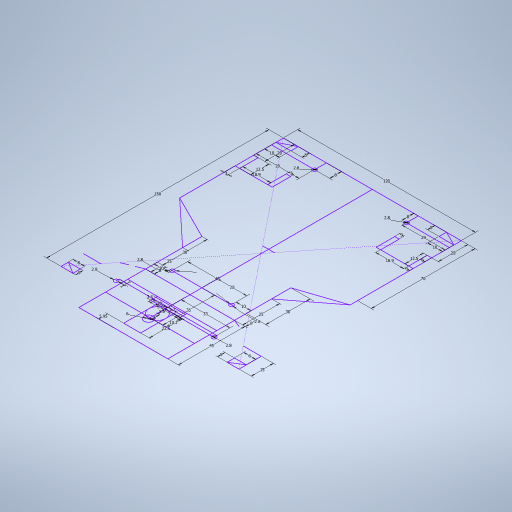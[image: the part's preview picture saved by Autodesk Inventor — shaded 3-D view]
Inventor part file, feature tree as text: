
AUTODESK INVENTOR PART (.ipt)
format: ipt  version: 2023 (Build 270158000, 158)  size: 318,976 bytes
history: native  units: in
note: dims shown in document units (in); Inventor stores cm internally (conversion verified against a paired STEP export)
features: sketch x1
ambient origin geometry x8: Origin, YZ Plane, XZ Plane, XY Plane, X Axis, Y Axis, Z Axis, Center Point
feature tree (1):
  sketch  "Sketch1"  dims[d0=4.7244in d1=5.9055in d2=0.7874in d3=0.1181in d4=0.1181in d5=0.4921in d6=0.7441in d7=0.1181in d8=0.4016in d9=1.2992in d11=0.1102in d12=0.1102in d13=1.378in d14=0.7874in d15=1.5748in d16=0.1102in d17=0.1102in d18=2.7559in d19=0.5906in d20=0.3937in d21=0.3937in d22=1.1811in d23=1.1811in d24=0.315in d25=0.315in d26=0.7874in d27=0.1181in d28=0.4921in d29=0.7441in d30=0.1181in d31=0.315in d32=0.1969in d33=0.315in d34=0.1969in d35=0.3937in d36=0.1969in d37=0.3937in d38=0.1969in d39=0.0787in d40=0.3937in d41=0.7874in d42=0.1378in d43=0.9843in d44=0.9843in d45=1.1417in d46=0.315in d47=1.1417in d48=0.315in d49=0.1102in d50=0.1102in d51=0.2244in d52=0.2244in d53=0.8858in d54=1.7717in d55=0.2343in d56=0.2165in d57=0.2362in d58=0.2362in]
